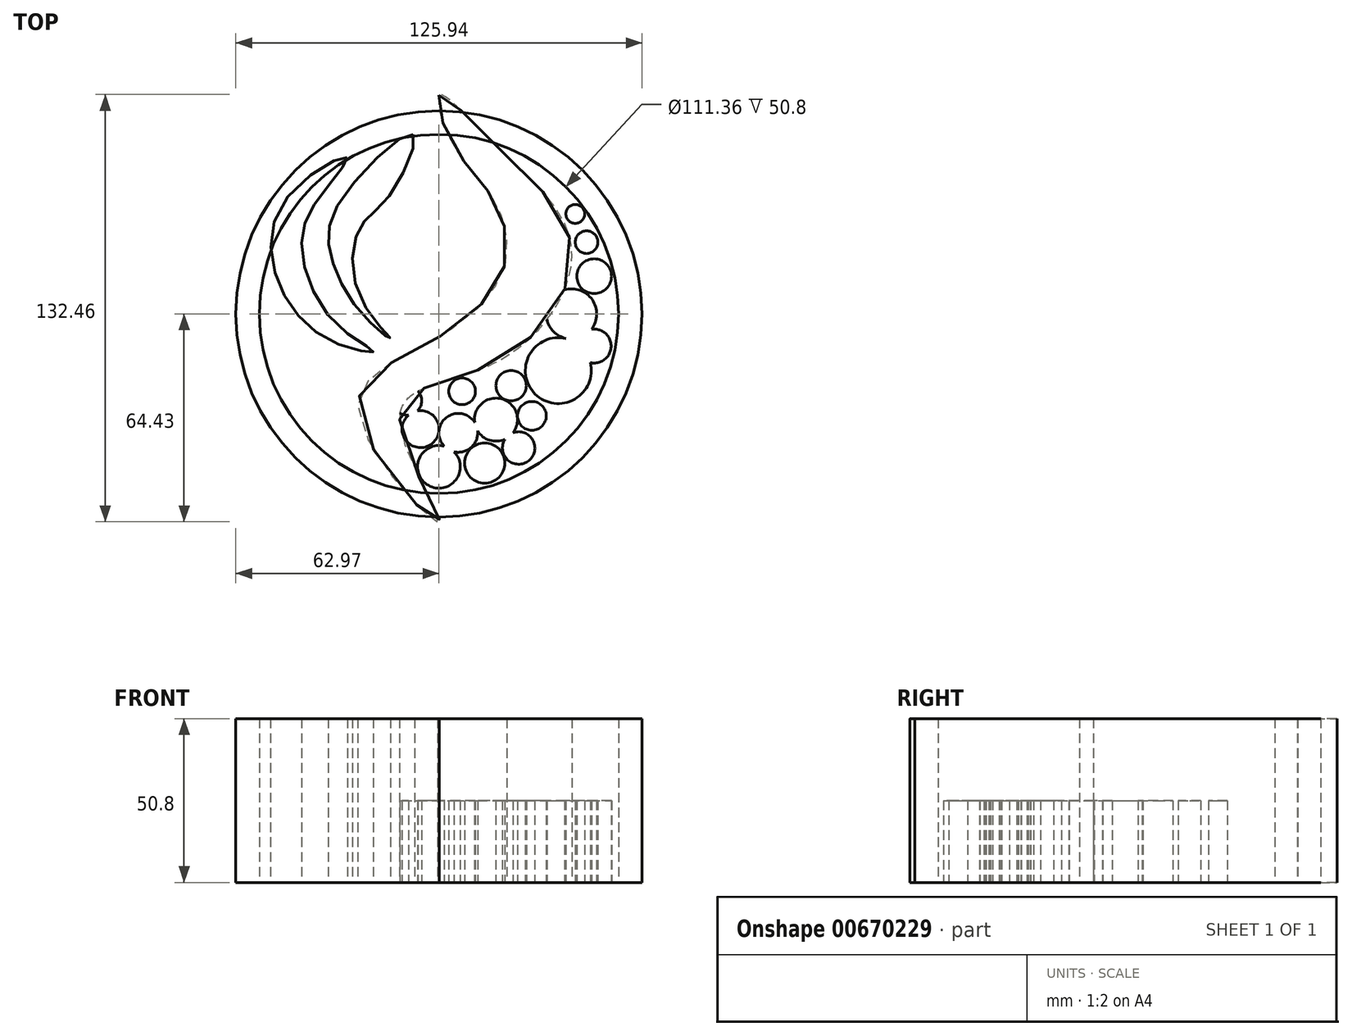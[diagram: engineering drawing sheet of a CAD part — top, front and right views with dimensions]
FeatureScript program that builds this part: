
annotation { "Feature Type Name" : "Feature", "Feature Type Description" : "" }
export const myFeature = defineFeature(function(context is Context, id is Id, definition is map)
    precondition{}
    {
        {
            var Q0;
            Q0=qCreatedBy(makeId("Top.planeOp"),FACE);
            var sketch = newSketch(context, id + "F0", { "sketchPlane" : qUnion([Q0])});
            skFitSpline(sketch, "E0", {"points": [v(0, 67.87) * mm, v(4.24, 52.66) * mm, v(17.11, 35.1) * mm, v(20.04, 14.04) * mm, v(-2.78, -8.78) * mm, v(-25.01, -30.42) * mm, v(0, -64.36) * mm, v(-12.14, -31.6) * mm, v(17.11, -15.21) * mm, v(41.1, 20.48) * mm, v(15.36, 54.41) * mm, v(0, 67.87) * mm]});
            skFitSpline(sketch, "E1", {"points": [v(-8.04, 55.58) * mm, v(-15.65, 36.28) * mm, v(-24.43, 26.91) * mm, v(-24.43, 5.27) * mm, v(-15.07, -7.6) * mm, v(-23.84, 0) * mm, v(-33.79, 19.3) * mm, v(-29.7, 36.28) * mm, v(-8.04, 55.58) * mm]});
            skFitSpline(sketch, "E2", {"points": [v(-28.52, 48.56) * mm, v(-36.13, 37.45) * mm, v(-42.56, 21.06) * mm, v(-31.45, -3.51) * mm, v(-20.33, -11.7) * mm, v(-33.79, -8.2) * mm, v(-49.59, 9.36) * mm, v(-47.83, 35.1) * mm, v(-28.52, 48.56) * mm]});
            skSolve(sketch);
        }
        {
            var Q0;
            Q0 = qSketchRegion(id + "F0", true);
            extrude(context, id + "F1", {"entities" : qUnion([Q0]), "depth" : 50.8 * mm, "offsetDistance" : 25.4 * mm});
        }
        {
            var Q0;
            Q0=qCreatedBy(makeId("Top.planeOp"),FACE);
            var sketch = newSketch(context, id + "F2", { "sketchPlane" : qUnion([Q0])});
            skCircle(sketch, "E3", {"center": v(0, 0) * mm, "radius": 62.97 * mm});
            skCircle(sketch, "E4", {"center": v(0, 0) * mm, "radius": 55.68 * mm});
            skSolve(sketch);
        }
        {
            var Q0;
            Q0 = qSketchRegion(id + "F2", true);
            extrude(context, id + "F3", {"entities" : qUnion([Q0]), "depth" : 50.8 * mm, "offsetDistance" : 25.4 * mm});
        }
        {
            var Q0;
            Q0=qCreatedBy(makeId("Top.planeOp"),FACE);
            var sketch = newSketch(context, id + "F4", { "sketchPlane" : qUnion([Q0])});
            skCircle(sketch, "E5", {"center": v(-9.8, -26.91) * mm, "radius": 4.46 * mm});
            skCircle(sketch, "E6", {"center": v(0, -47.4) * mm, "radius": 6.6 * mm});
            skCircle(sketch, "E7", {"center": v(14.19, -46.22) * mm, "radius": 6.22 * mm});
            skCircle(sketch, "E8", {"center": v(6, -36.86) * mm, "radius": 6.02 * mm});
            skCircle(sketch, "E9", {"center": v(17.7, -32.76) * mm, "radius": 6.67 * mm});
            skCircle(sketch, "E10", {"center": v(24.72, -41.54) * mm, "radius": 5.03 * mm});
            skCircle(sketch, "E11", {"center": v(28.82, -31.6) * mm, "radius": 4.46 * mm});
            skCircle(sketch, "E12", {"center": v(22.38, -22.23) * mm, "radius": 4.72 * mm});
            skCircle(sketch, "E13", {"center": v(7.17, -23.99) * mm, "radius": 4.14 * mm});
            skCircle(sketch, "E14", {"center": v(-5.7, -35.7) * mm, "radius": 5.74 * mm});
            skCircle(sketch, "E15", {"center": v(37, -17.55) * mm, "radius": 10.22 * mm});
            skCircle(sketch, "E16", {"center": v(41.1, 0) * mm, "radius": 7.8 * mm});
            skCircle(sketch, "E17", {"center": v(48.12, 11.7) * mm, "radius": 5.4 * mm});
            skCircle(sketch, "E18", {"center": v(45.78, 22.23) * mm, "radius": 3.51 * mm});
            skCircle(sketch, "E19", {"center": v(42.27, 31) * mm, "radius": 2.93 * mm});
            skCircle(sketch, "E20", {"center": v(48.12, -9.95) * mm, "radius": 5.27 * mm});
            skSolve(sketch);
        }
        {
            var Q0;
            Q0 = qSketchRegion(id + "F4", true);
            extrude(context, id + "F5", {"entities" : qUnion([Q0]), "operationType" : NewBodyOperationType.ADD, "depth" : 25.4 * mm, "offsetDistance" : 25.4 * mm});
        }
    });
